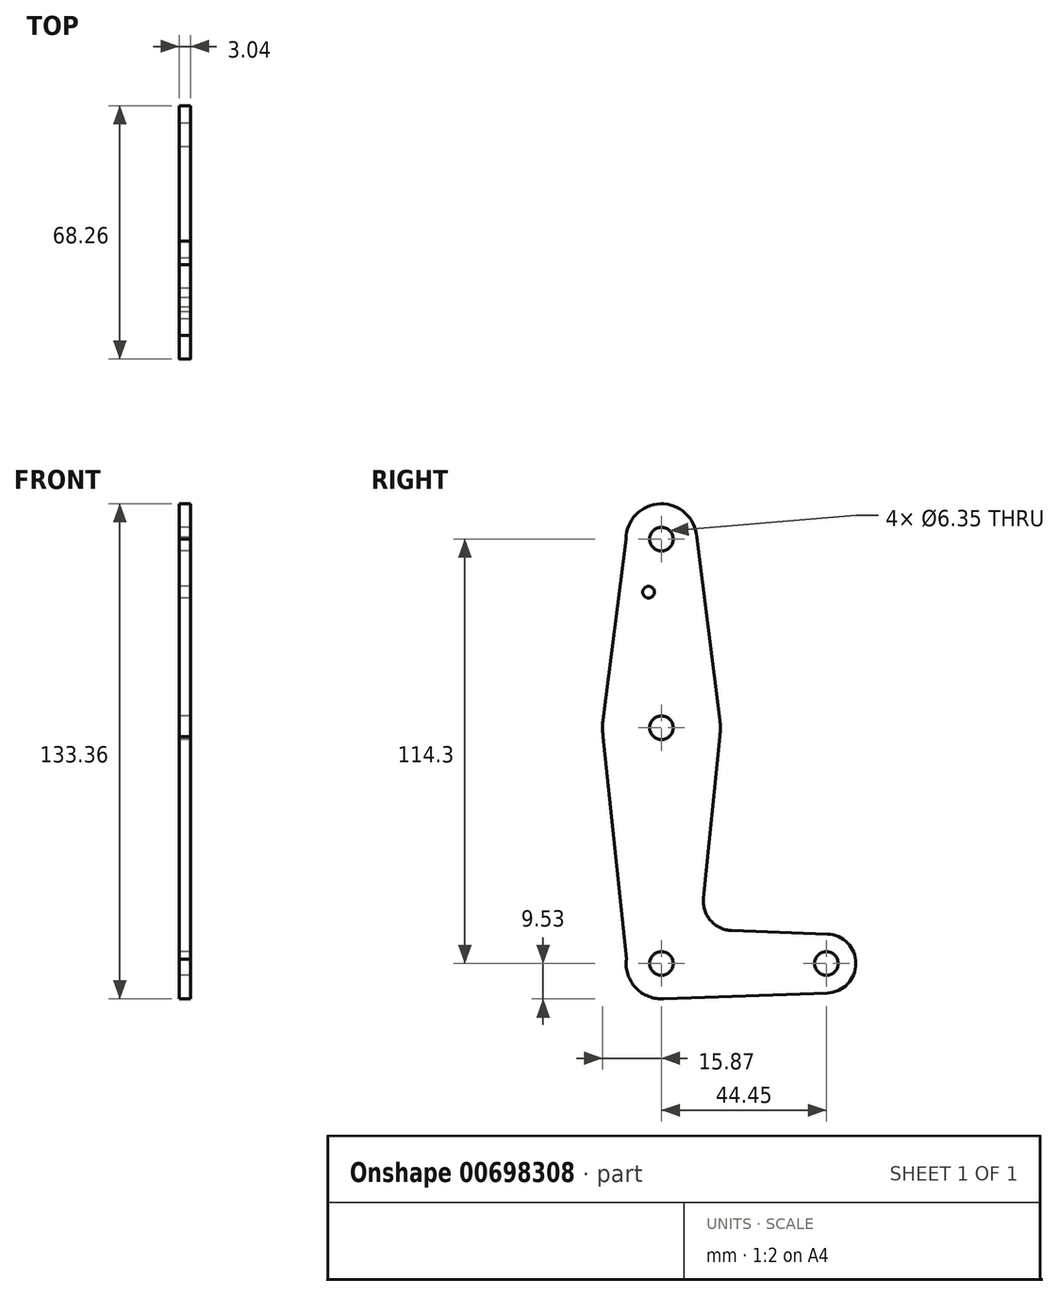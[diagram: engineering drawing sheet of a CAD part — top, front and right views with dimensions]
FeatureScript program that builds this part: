
annotation { "Feature Type Name" : "Feature", "Feature Type Description" : "" }
export const myFeature = defineFeature(function(context is Context, id is Id, definition is map)
    precondition{}
    {
        {
            var Q0;
            Q0=qCreatedBy(makeId("Right.planeOp"),FACE);
            var sketch = newSketch(context, id + "F0", { "sketchPlane" : qUnion([Q0])});
            skLineSegment(sketch, "E0", {"start": v(0, 63.5) * mm, "end": v(0, 114.3) * mm});
            skCircle(sketch, "E1", {"center": v(0, 114.3) * mm, "radius": 9.53 * mm});
            skCircle(sketch, "E2", {"center": v(0, 63.5) * mm, "radius": 15.88 * mm});
            skCircle(sketch, "E3", {"center": v(44.45, 0) * mm, "radius": 7.94 * mm});
            skLineSegment(sketch, "E4", {"start": v(-9.53, 114.3) * mm, "end": v(-15.75, 65.5) * mm});
            skLineSegment(sketch, "E5", {"start": v(9.5, 114.88) * mm, "end": v(15.75, 65.5) * mm});
            skLineSegment(sketch, "E6", {"start": v(18.96, 8.85) * mm, "end": v(44.73, 7.93) * mm});
            skLineSegment(sketch, "E7", {"start": v(15.85, 62.61) * mm, "end": v(11.34, 17.59) * mm});
            skLineSegment(sketch, "E8", {"start": v(0, -9.53) * mm, "end": v(44.73, -7.93) * mm});
            skCircle(sketch, "E9", {"center": v(-3.47, 100.03) * mm, "radius": 1.59 * mm});
            skCircle(sketch, "E10", {"center": v(0, 114.3) * mm, "radius": 3.18 * mm});
            skCircle(sketch, "E11", {"center": v(0, 63.5) * mm, "radius": 3.18 * mm});
            skCircle(sketch, "E12", {"center": v(0, 0) * mm, "radius": 3.18 * mm});
            skCircle(sketch, "E13", {"center": v(44.45, 0) * mm, "radius": 3.18 * mm});
            skPoint(sketch, "E14.newPointA", {"position": v(0, 9.53) * mm});
            skPoint(sketch, "E14.newPointB", {"position": v(9.57, 0) * mm});
            skArc(sketch, "E14.filletArc", {"start": v(11.34, 17.59) * mm, "mid": v(13.26, 11.57) * mm, "end": v(18.96, 8.85) * mm});
            skLineSegment(sketch, "E15", {"start": v(-15.7, 61.13) * mm, "end": v(-9.46, 1.1) * mm});
            skCircle(sketch, "E16", {"center": v(0, 0) * mm, "radius": 9.53 * mm});
            skSolve(sketch);
        }
        {
            var Q0;
            Q0 = qSketchRegion(id + "F0", true);
            extrude(context, id + "F1", {"entities" : qUnion([Q0]), "depth" : 3.04 * mm, "offsetDistance" : 25.4 * mm});
        }
    });
